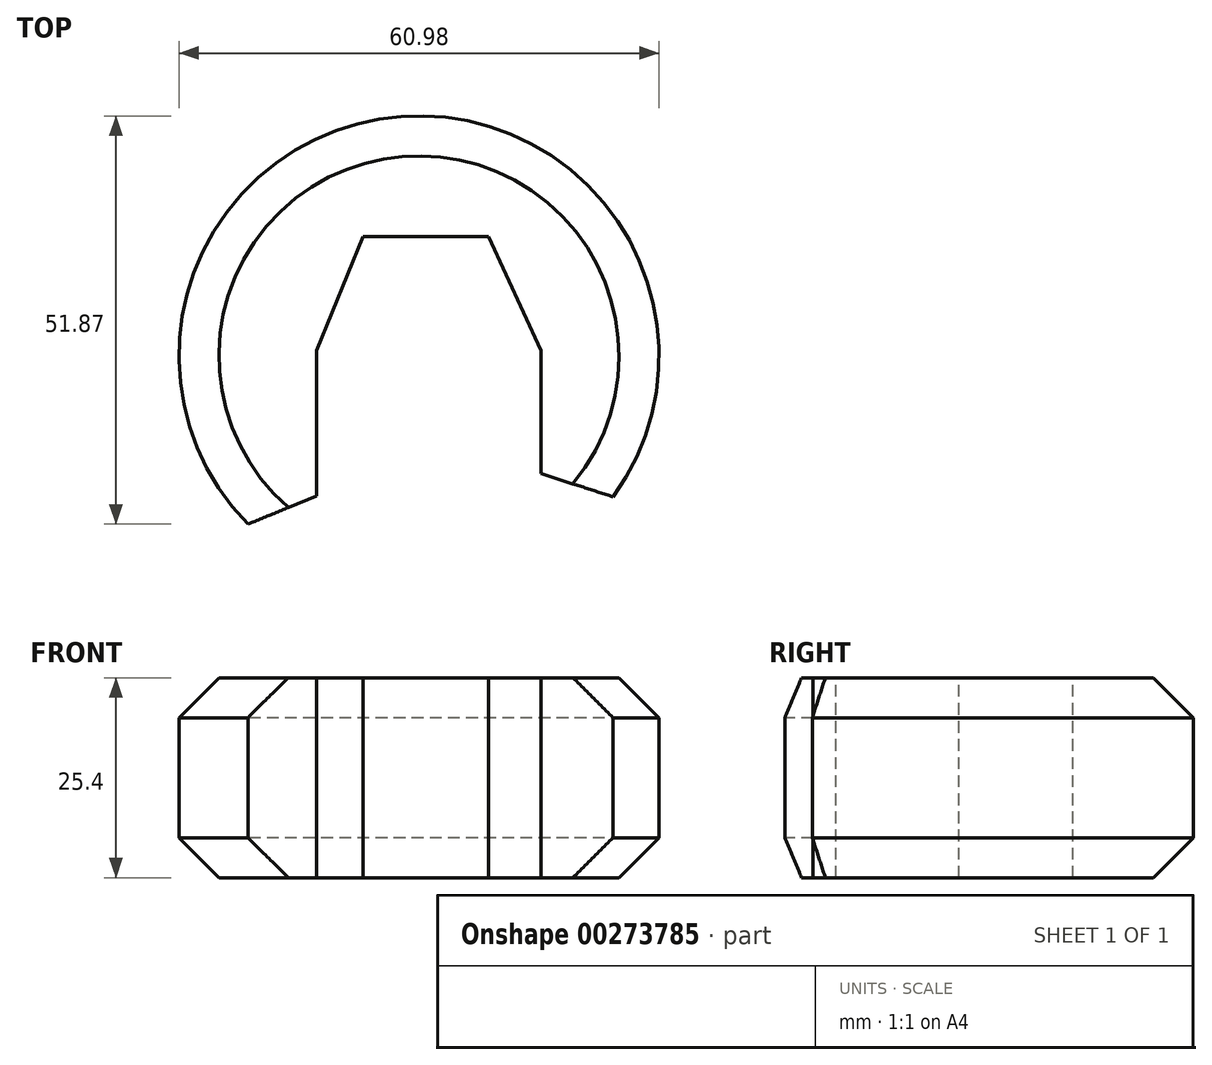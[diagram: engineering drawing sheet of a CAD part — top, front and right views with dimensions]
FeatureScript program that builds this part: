
annotation { "Feature Type Name" : "Feature", "Feature Type Description" : "" }
export const myFeature = defineFeature(function(context is Context, id is Id, definition is map)
    precondition{}
    {
        {
            var Q0;
            Q0=qCreatedBy(makeId("Top.planeOp"),FACE);
            var sketch = newSketch(context, id + "F0", { "sketchPlane" : qUnion([Q0])});
            skCircle(sketch, "E0", {"center": v(0, -76.22) * mm, "radius": 30.49 * mm});
            skLineSegment(sketch, "E1", {"start": v(-30.48, -75.87) * mm, "end": v(-30.48, -59.88) * mm});
            skLineSegment(sketch, "E2", {"start": v(-30.48, -59.88) * mm, "end": v(-23.6, -41.01) * mm});
            skLineSegment(sketch, "E3", {"start": v(-23.6, -41.01) * mm, "end": v(-12.34, -17.78) * mm});
            skLineSegment(sketch, "E4", {"start": v(-12.34, -17.78) * mm, "end": v(-12.34, 50.81) * mm});
            skLineSegment(sketch, "E5", {"start": v(-12.34, 50.81) * mm, "end": v(0, 50.81) * mm});
            skLineSegment(sketch, "E6", {"start": v(0, 50.81) * mm, "end": v(0, -45.73) * mm});
            skLineSegment(sketch, "E7", {"start": v(0, 50.81) * mm, "end": v(0, -76.22) * mm, "construction": true});
            skSolve(sketch);
        }
        {
            var Q0;
            {var subQ0=sQuery(id+"F0.wireOp",EDGE,"E0");var subQ1=makeQuery(id+"F0.imprint","INTERSECT",VERTEX,{"derivedFrom":[subQ0,sQuery(id+"F0.wireOp",EDGE,"E1")]});Q0=makeQuery(id+"F0.imprint","IMPRINT",FACE,{"disambiguationData":[TD([[makeQuery(id+"F0.imprint","IMPRINT",EDGE,{"disambiguationData":[TD([[subQ1,1.0]])],"derivedFrom":subQ0}),1.0]])]});}
            extrude(context, id + "F1", {"entities" : qUnion([Q0]), "depth" : 25.4 * mm});
        }
        {
            var Q0;
            Q0=makeQuery(id+"F1.opExtrude","CAP_FACE",FACE,{"disambiguationData":[OSD([sQuery(id+"F0.wireOp",EDGE,"E0")])],"isStart":false});
            var sketch = newSketch(context, id + "F2", { "sketchPlane" : qUnion([Q0])});
            skLineSegment(sketch, "E8", {"start": v(-13.03, -103.78) * mm, "end": v(-13.03, -75.53) * mm});
            skLineSegment(sketch, "E9", {"start": v(-13.03, -75.53) * mm, "end": v(-7.1, -61.03) * mm});
            skLineSegment(sketch, "E10", {"start": v(-7.1, -61.03) * mm, "end": v(8.82, -61.03) * mm});
            skLineSegment(sketch, "E11", {"start": v(8.82, -61.03) * mm, "end": v(15.48, -75.53) * mm});
            skLineSegment(sketch, "E12", {"start": v(15.48, -75.53) * mm, "end": v(15.48, -102.48) * mm});
            skLineSegment(sketch, "E13", {"start": v(-13.03, -103.78) * mm, "end": v(-13.03, -110.22) * mm});
            skLineSegment(sketch, "E14", {"start": v(-13.03, -110.22) * mm, "end": v(15.24, -110.22) * mm});
            skLineSegment(sketch, "E15", {"start": v(15.24, -110.22) * mm, "end": v(15.48, -102.48) * mm});
            skSolve(sketch);
        }
        {
            var Q0;
            {var subQ0=sQuery(id+"F2.wireOp",EDGE,"E8");Q0=makeQuery(id+"F2.imprint","IMPRINT",FACE,{"disambiguationData":[TD([[makeQuery(id+"F2.imprint","IMPRINT",EDGE,{"derivedFrom":subQ0}),-1.0]])]});}
            var Q1;
            {var subQ0=sQuery(id+"F2.wireOp",EDGE,"E13");Q1=makeQuery(id+"F2.imprint","IMPRINT",FACE,{"disambiguationData":[TD([[makeQuery(id+"F2.imprint","IMPRINT",EDGE,{"derivedFrom":subQ0}),1.0]])]});}
            extrude(context, id + "F3", {"entities" : qUnion([Q0, Q1]), "operationType" : NewBodyOperationType.REMOVE, "oppositeDirection" : true, "depth" : 25.4 * mm, "hasSecondDirection" : true, "secondDirectionOppositeDirection" : false, "secondDirectionDepth" : 25.4 * mm});
        }
        {
            var Q0;
            Q0=makeQuery(id+"F1.opExtrude","SWEPT_FACE",FACE,{"disambiguationData":[OSD([sQuery(id+"F0.wireOp",EDGE,"E0")])]});
            chamfer(context, id + "F4", {"entities" : qUnion([Q0]), "width" : 5.08 * mm, "tangentPropagation" : true});
        }
    });
